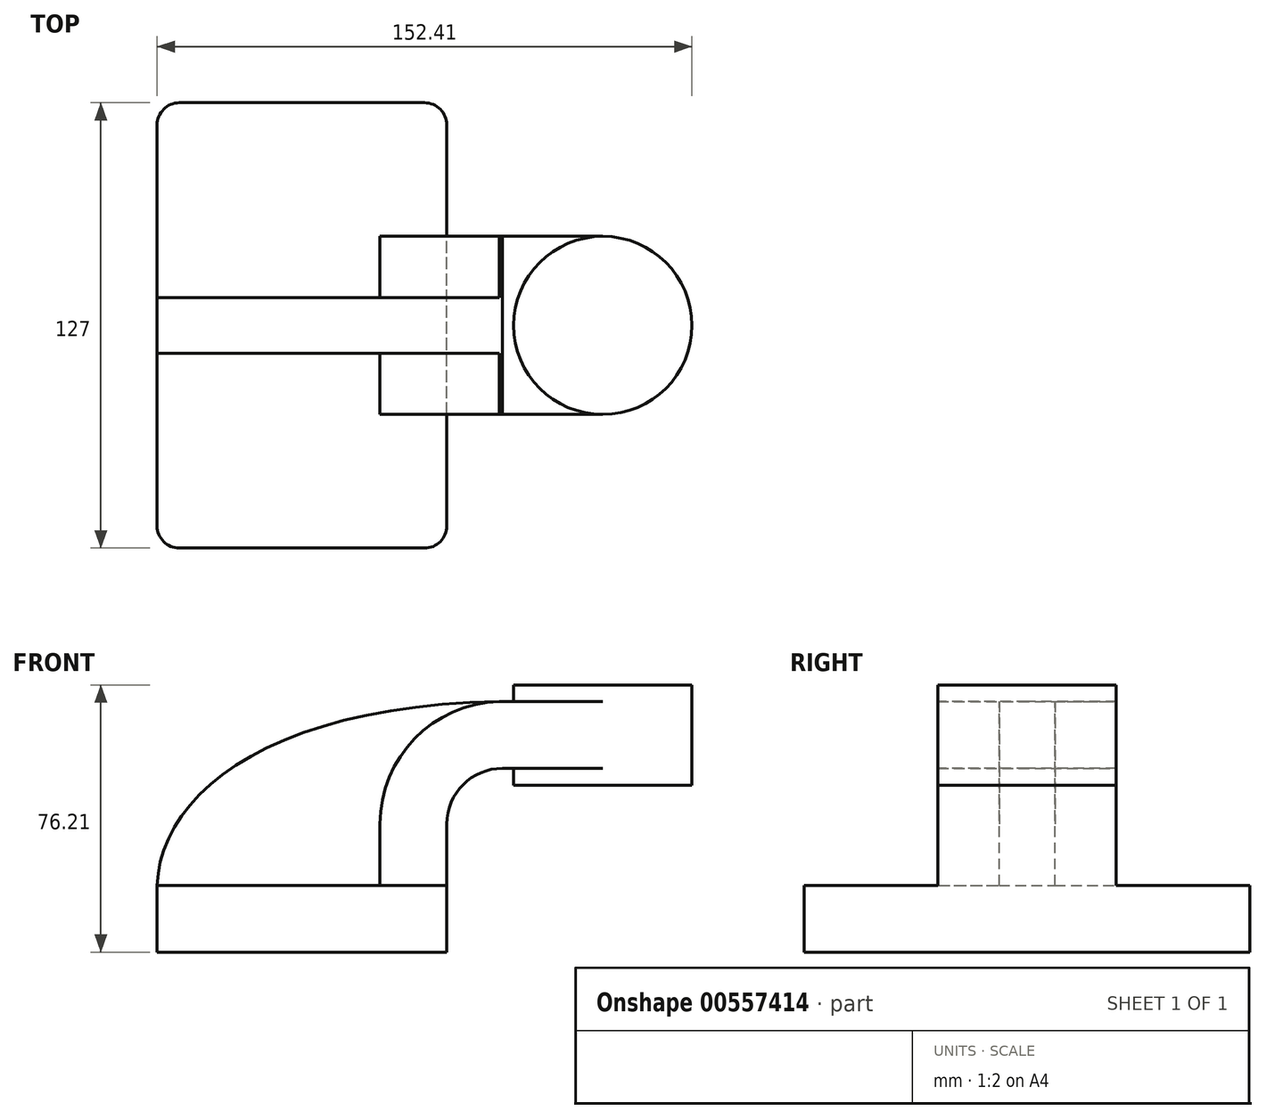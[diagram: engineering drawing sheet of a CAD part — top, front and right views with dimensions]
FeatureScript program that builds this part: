
annotation { "Feature Type Name" : "Feature", "Feature Type Description" : "" }
export const myFeature = defineFeature(function(context is Context, id is Id, definition is map)
    precondition{}
    {
        {
            var Q0;
            Q0=qCreatedBy(makeId("Front.planeOp"),FACE);
            var sketch = newSketch(context, id + "F0", { "sketchPlane" : qUnion([Q0])});
            skLineSegment(sketch, "E0.bottom", {"start": v(41.28, 9.53) * mm, "end": v(-41.28, 9.53) * mm});
            skLineSegment(sketch, "E0.top", {"start": v(41.28, -9.52) * mm, "end": v(-41.28, -9.52) * mm});
            skLineSegment(sketch, "E0.left", {"start": v(41.28, 9.53) * mm, "end": v(41.28, -9.52) * mm});
            skLineSegment(sketch, "E0.right", {"start": v(-41.28, 9.53) * mm, "end": v(-41.28, -9.52) * mm});
            skPoint(sketch, "E0.middle", {"position": v(0, 0) * mm});
            skLineSegment(sketch, "E1.bottom", {"start": v(111.13, 66.68) * mm, "end": v(60.33, 66.68) * mm});
            skLineSegment(sketch, "E1.top", {"start": v(111.13, 38.1) * mm, "end": v(60.33, 38.1) * mm});
            skLineSegment(sketch, "E1.left", {"start": v(111.13, 66.68) * mm, "end": v(111.13, 38.1) * mm});
            skLineSegment(sketch, "E1.right", {"start": v(60.33, 66.68) * mm, "end": v(60.33, 38.1) * mm});
            skPoint(sketch, "E1.middle", {"position": v(85.73, 52.39) * mm});
            skLineSegment(sketch, "E2", {"start": v(41.28, 9.53) * mm, "end": v(41.28, 27) * mm});
            skArc(sketch, "E3", {"start": v(41.28, 27) * mm, "mid": v(45.92, 38.23) * mm, "end": v(57.15, 42.88) * mm});
            skLineSegment(sketch, "E4", {"start": v(57.15, 42.88) * mm, "end": v(85.73, 42.88) * mm});
            skLineSegment(sketch, "E5.0", {"start": v(57.15, 61.93) * mm, "end": v(85.73, 61.93) * mm});
            skArc(sketch, "E5.1", {"start": v(22.23, 27) * mm, "mid": v(32.45, 51.7) * mm, "end": v(57.15, 61.93) * mm});
            skLineSegment(sketch, "E5.2", {"start": v(22.22, 9.53) * mm, "end": v(22.22, 27) * mm});
            skLineSegment(sketch, "E6", {"start": v(85.73, 38.1) * mm, "end": v(85.73, 66.68) * mm});
            skFitSpline(sketch, "E7", {"points": [v(-41.28, 9.52) * mm, v(57.15, 61.93) * mm], "startDerivative": vector(2.55, 77.82) * mm, "endDerivative": vector(197.93, 2.28) * mm});
            skSolve(sketch);
        }
        {
            var Q0;
            Q0=makeQuery(id+"F0.imprint","IMPRINT",FACE,{"disambiguationData":[TD([[makeQuery(id+"F0.imprint","IMPRINT",EDGE,{"derivedFrom":sQuery(id+"F0.wireOp",EDGE,"E0.top")}),-1.0]])]});
            extrude(context, id + "F1", {"entities" : qUnion([Q0]), "endBound" : BoundingType.SYMMETRIC, "depth" : 127 * mm, "offsetDistance" : 25.4 * mm});
        }
        {
            var Q0;
            {var subQ0=sQuery(id+"F0.wireOp",EDGE,"E5.0");var subQ1=sQuery(id+"F0.wireOp",EDGE,"E1.right");var subQ2=makeQuery(id+"F0.imprint","INTERSECT",VERTEX,{"derivedFrom":[subQ1,subQ0]});Q0=makeQuery(id+"F0.imprint","IMPRINT",FACE,{"disambiguationData":[TD([[makeQuery(id+"F0.imprint","IMPRINT",EDGE,{"disambiguationData":[TD([[subQ2,-1.0]])],"derivedFrom":subQ1}),1.0]])]});}
            var Q1;
            {var subQ1=sQuery(id+"F0.wireOp",EDGE,"E2");Q1=makeQuery(id+"F0.imprint","IMPRINT",FACE,{"disambiguationData":[TD([[makeQuery(id+"F0.imprint","IMPRINT",EDGE,{"derivedFrom":subQ1}),1.0]])]});}
            extrude(context, id + "F2", {"entities" : qUnion([Q0, Q1]), "operationType" : NewBodyOperationType.ADD, "endBound" : BoundingType.SYMMETRIC, "depth" : 50.8 * mm, "offsetDistance" : 25.4 * mm});
        }
        {
            var Q0;
            {var subQ3=sQuery(id+"F0.wireOp",EDGE,"E5.2");Q0=makeQuery(id+"F0.imprint","IMPRINT",FACE,{"disambiguationData":[TD([[makeQuery(id+"F0.imprint","IMPRINT",EDGE,{"derivedFrom":subQ3}),1.0]])]});}
            extrude(context, id + "F3", {"entities" : qUnion([Q0]), "operationType" : NewBodyOperationType.ADD, "endBound" : BoundingType.SYMMETRIC, "depth" : 15.88 * mm, "offsetDistance" : 25.4 * mm});
        }
        {
            var Q0;
            {var subQ0=sQuery(id+"F0.wireOp",EDGE,"E1.left");Q0=makeQuery(id+"F0.imprint","IMPRINT",FACE,{"disambiguationData":[TD([[makeQuery(id+"F0.imprint","IMPRINT",EDGE,{"derivedFrom":subQ0}),-1.0]])]});}
            var Q1;
            Q1=sQuery(id+"F0.wireOp",EDGE,"E6");
            revolve(context, id + "F4", {"operationType" : NewBodyOperationType.ADD, "entities" : qUnion([Q0]), "axis" : qUnion([Q1]), "revolveType" : RevolveType.FULL});
        }
        {
            var Q0;
            Q0=makeQuery(id+"F1.opExtrude","CAP_EDGE",EDGE,{"disambiguationData":[OSD([sQuery(id+"F0.wireOp",EDGE,"E0.right")])],"isStart":false});
            var Q1;
            Q1=makeQuery(id+"F1.opExtrude","CAP_EDGE",EDGE,{"disambiguationData":[OSD([sQuery(id+"F0.wireOp",EDGE,"E0.left")])],"isStart":false});
            var Q2;
            Q2=makeQuery(id+"F1.opExtrude","CAP_EDGE",EDGE,{"disambiguationData":[OSD([sQuery(id+"F0.wireOp",EDGE,"E0.left")])],"isStart":true});
            var Q3;
            Q3=makeQuery(id+"F1.opExtrude","CAP_EDGE",EDGE,{"disambiguationData":[OSD([sQuery(id+"F0.wireOp",EDGE,"E0.right")])],"isStart":true});
            fillet(context, id + "F5", {"entities" : qUnion([Q0, Q1, Q2, Q3]), "radius" : 6.35 * mm, "tangentPropagation" : true, "allowEdgeOverflow" : false});
        }
    });
